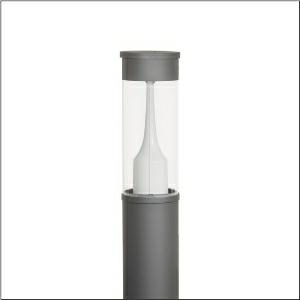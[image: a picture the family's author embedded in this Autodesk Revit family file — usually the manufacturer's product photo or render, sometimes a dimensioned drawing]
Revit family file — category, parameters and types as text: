
# Revit family: city-light_260_iq___p1_0a_5xa5295ff14h_c360
name_source: partatom
category: Lighting Fixtures
units: mm (PartAtom-declared; Revit-internal decimal feet)

## family parameters
Cut with Voids When Loaded = No
Host = Face
Light Source = No
Part Type = Normal
Room Calculation Point = No
Round Connector Dimension = Use Diameter
Shared = No

## types (1)
- --- (1 x LED, 1510 lm, 10.5 W, 3000K)
    Apparent Load = 11 VA
    CIE Flux Codes = 32 61 90 93 100
    Color Rendering = 70
    Color Temperature = 3000K
    Default Elevation = 1800 mm
    Description = City-Light 260 iQ, light pillar, Module 540 iQ-SR, primary light control with 3 zone facetted reflector, of plastic, silver coated, highly specular, structured, primary optical cover: cover, of PMMA, transparent, light distribution: P1.0a, primary light characteristic: strongly asymmetric, LED, High Power LED, rated luminous flux: 1.510lm, luminous efficacy: 144lm/W, light colour: 730, colour temperature: 3000K, control gear: iQ Street-Remote, control: Auto-Match, Temp-Guard, Lumen-Switch, Night-Set, Smart-Wire, Light-Fading, Desk-Remote (wireless, voltage-free reading and setting of iQ features in the workshop via application-optimized NFC function/RFID function), optimised constant luminous flux control (CLO 2.0), Street-Remote, pre-setting: logarithmic dimming characteristic, with terminal, 6-pole, max. 2.5mm², mains connection: 230..240V, AC, 50/60Hz, start of lifetime: 11W, end of service life: 11W, reduction: 5W, luminaire housing, cylindrical, of extruded aluminium section, coated, Siteco® metallic grey (DB 702S), length: 2.600mm, diameter: 200mm, Module 540 iQ-SR, traffic white (RAL 9016), equipment: standard, protection rating (complete): IP65, insulation class (complete): insulation class II (safety insulation), certification: CE, ENEC, VDE, packaging unit: 1 piece

Light Distribution: P1.0a
    Height = 500 mm
    Lamp = 1 x LED
    Lamp Light Flux = 1510 lm
    Lamp Power = 10.5 W
    Lamp count = 1
    Length = 200 mm  [stored 0.656168 ft]
    Luminous efficacy = 144 lm/W
    Manufacturer = Siteco
    ModVariant = No
    Model = 5XA5295FF14H
    Mounting Place = Floor
    Mounting Type = Freestanding
    Number of Poles = 1
    OnlyDefault = Yes
    Power Factor = 1
    Product Name = City-Light 260 iQ | P1.0a
    Product group = light pillar
    ProductGroupID = 1301
    Protection Class = Protection class II
    Protection Degree = IP 65
    RLX_Detail_Level = 1
    RLX_Emergency_Light_Flux = 0 lm
    RLX_Emergency_Type = 0
    RLX_Emergency_Type_DB = No
    RlxData = <blob elided: 52653 chars, md5=eec34113>
    Socket = socket
    Standby Power = 0 W
    System Light Flux = 1510 lm
    System Power = 11 W
    Type Comments = factory setting: luminous flux: 100 % | dim-lin: 254 | 419 mA
    Type Image = l_1006918.jpg
    URL = http://relux.com
    VarID = @adj_180963
    Voltage = 0 V
    Weight = 0.00 kg
    Width = 0 mm  [stored 0 ft]

note: [stored X ft] marks values corroborated as IEEE doubles in the binary element streams (Revit-internal decimal feet)

## geometry (parser evidence)
native form markers: Blend x4, Sweep x13
no freeform markers — native parametric forms only
